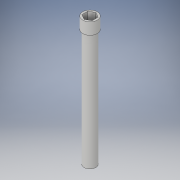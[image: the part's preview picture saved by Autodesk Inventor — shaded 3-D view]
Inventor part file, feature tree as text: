
AUTODESK INVENTOR PART (.ipt)
format: ipt  version: 2018 (Build 220112000, 112)  size: 109,568 bytes
history: native  units: in
note: dims shown in document units (in); Inventor stores cm internally (conversion verified against a paired STEP export)
features: extrude x3, sketch x3
ambient origin geometry x8: Origin, YZ Plane, XZ Plane, XY Plane, X Axis, Y Axis, Z Axis, Center Point
bodies: Solid1 (feature_tree)
feature tree (6):
  extrude  "Extrusion1"  Depth=2.0in TaperAngle=0.0deg
  extrude  "Extrusion2"  Depth=0.2in TaperAngle=0.0deg
  extrude  "Extrusion3"  [1 undecoded]
  sketch  "Sketch1"  dims[d0=0.2031in d1=2.0in d2=0.0in]
  sketch  "Sketch2"  dims[d3=0.25in d4=0.2in d5=0.0in]
  sketch  "Sketch3"  dims[d6=0.15in d7=0.0in]
note: 1 required parameter value undecoded (feature->parameter linkage not recoverable at this tier; creation-order binding heuristic only, values carry confidence <= 0.55)
